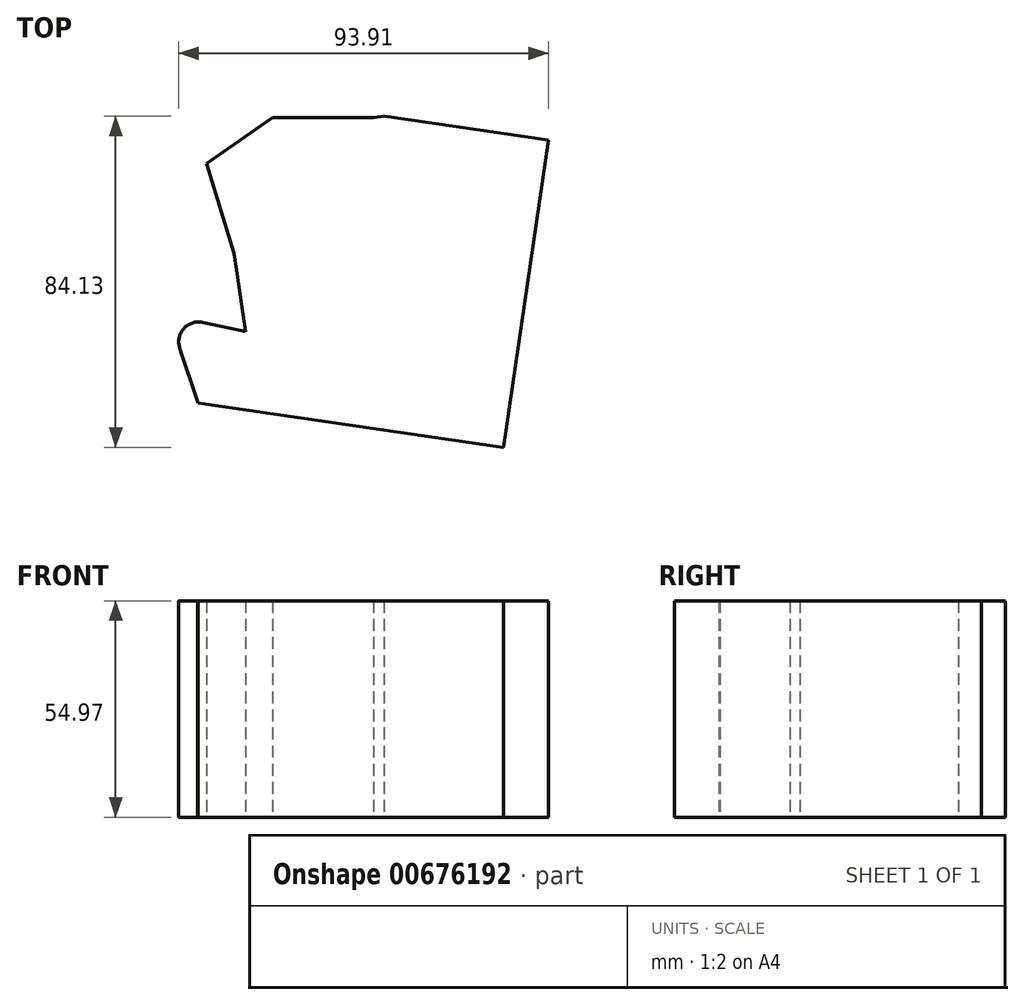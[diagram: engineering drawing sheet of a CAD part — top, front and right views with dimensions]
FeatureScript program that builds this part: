
annotation { "Feature Type Name" : "Feature", "Feature Type Description" : "" }
export const myFeature = defineFeature(function(context is Context, id is Id, definition is map)
    precondition{}
    {
        {
            var Q0;
            Q0=qCreatedBy(makeId("Top.planeOp"),FACE);
            var sketch = newSketch(context, id + "F0", { "sketchPlane" : qUnion([Q0])});
            skLineSegment(sketch, "E0", {"start": v(-47.16, -24.8) * mm, "end": v(30.4, -36.14) * mm});
            skLineSegment(sketch, "E1", {"start": v(30.4, -36.14) * mm, "end": v(41.8, 41.88) * mm});
            skLineSegment(sketch, "E2", {"start": v(41.8, 41.88) * mm, "end": v(0, 47.99) * mm});
            skLineSegment(sketch, "E3", {"start": v(0, 47.99) * mm, "end": v(-2.6, 47.69) * mm});
            skLineSegment(sketch, "E4", {"start": v(-2.6, 47.69) * mm, "end": v(-28.32, 47.69) * mm});
            skLineSegment(sketch, "E5", {"start": v(-28.32, 47.69) * mm, "end": v(-45.03, 36) * mm});
            skLineSegment(sketch, "E6", {"start": v(-45.03, 36) * mm, "end": v(-37.99, 12.7) * mm});
            skLineSegment(sketch, "E7", {"start": v(-37.99, 12.7) * mm, "end": v(-35.07, -6.74) * mm});
            skLineSegment(sketch, "E8", {"start": v(-35.07, -6.74) * mm, "end": v(-54.68, -2.48) * mm});
            skLineSegment(sketch, "E9", {"start": v(-54.68, -2.48) * mm, "end": v(-47.3, -24.54) * mm});
            skLineSegment(sketch, "E10", {"start": v(-47.3, -24.54) * mm, "end": v(-47.16, -24.8) * mm});
            skSolve(sketch);
        }
        {
            var Q0;
            Q0=makeQuery(id+"F0.imprint","IMPRINT",FACE,{"disambiguationData":[TD([[makeQuery(id+"F0.imprint","IMPRINT",EDGE,{"derivedFrom":sQuery(id+"F0.wireOp",EDGE,"E0")}),1.0]])]});
            extrude(context, id + "F1", {"entities" : qUnion([Q0]), "depth" : 54.97 * mm, "offsetDistance" : 25.4 * mm});
        }
        {
            var Q0;
            Q0=makeQuery(id+"F1.opExtrude","SWEPT_EDGE",EDGE,{"disambiguationData":[OSD([sQuery(id+"F0.wireOp",EDGE,"E6"),sQuery(id+"F0.wireOp",EDGE,"E7")])]});
            var Q1;
            Q1=makeQuery(id+"F1.opExtrude","SWEPT_EDGE",EDGE,{"disambiguationData":[OSD([sQuery(id+"F0.wireOp",EDGE,"E8"),sQuery(id+"F0.wireOp",EDGE,"E9")])]});
            fillet(context, id + "F2", {"entities" : qUnion([Q0, Q1]), "radius" : 5.08 * mm, "tangentPropagation" : true, "allowEdgeOverflow" : false});
        }
    });
